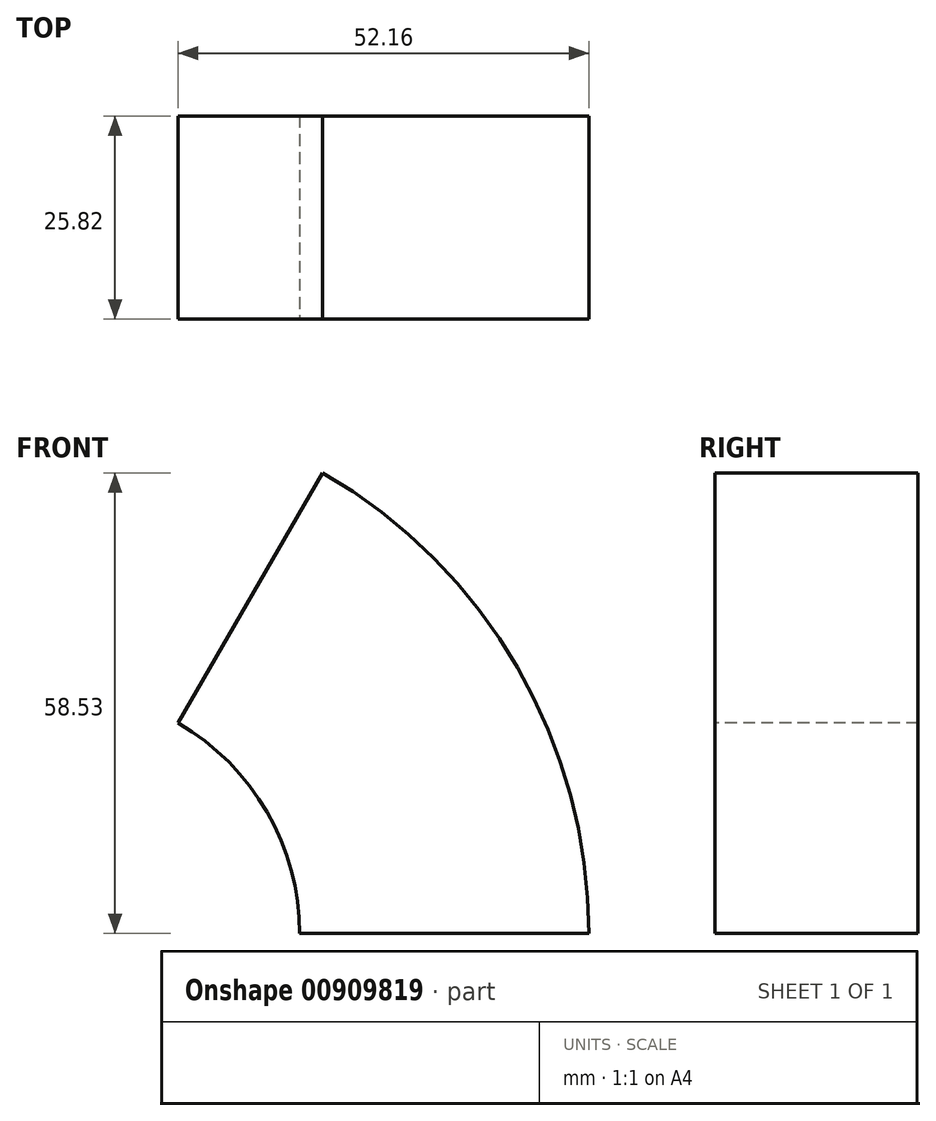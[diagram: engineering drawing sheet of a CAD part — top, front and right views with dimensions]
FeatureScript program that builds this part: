
annotation { "Feature Type Name" : "Feature", "Feature Type Description" : "" }
export const myFeature = defineFeature(function(context is Context, id is Id, definition is map)
    precondition{}
    {
        {
            var Q0;
            Q0=qCreatedBy(makeId("Top.planeOp"),FACE);
            var sketch = newSketch(context, id + "F0", { "sketchPlane" : qUnion([Q0])});
            skLineSegment(sketch, "E0.bottom", {"start": v(30.85, 0) * mm, "end": v(67.59, 0) * mm});
            skLineSegment(sketch, "E0.top", {"start": v(30.85, -25.82) * mm, "end": v(67.59, -25.82) * mm});
            skLineSegment(sketch, "E0.left", {"start": v(30.85, 0) * mm, "end": v(30.85, -25.82) * mm});
            skLineSegment(sketch, "E0.right", {"start": v(67.59, 0) * mm, "end": v(67.59, -25.82) * mm});
            skSolve(sketch);
        }
        {
            var Q0;
            Q0=qCreatedBy(makeId("Top.planeOp"),FACE);
            var sketch = newSketch(context, id + "F1", { "sketchPlane" : qUnion([Q0])});
            skLineSegment(sketch, "E1", {"start": v(0, -29.87) * mm, "end": v(0, 32.27) * mm});
            skSolve(sketch);
        }
        {
            var Q0;
            Q0=makeQuery(id+"F0.imprint","IMPRINT",FACE,{"disambiguationData":[TD([[makeQuery(id+"F0.imprint","IMPRINT",EDGE,{"derivedFrom":sQuery(id+"F0.wireOp",EDGE,"E0.bottom")}),-1.0]])]});
            var Q1;
            Q1=sQuery(id+"F1.wireOp",EDGE,"E1");
            revolve(context, id + "F2", {"surfaceOperationType" : NewSurfaceOperationType.NEW, "entities" : qUnion([Q0]), "axis" : qUnion([Q1]), "revolveType" : RevolveType.ONE_DIRECTION, "oppositeDirection" : true, "angle" : 60 * degree});
        }
    });
